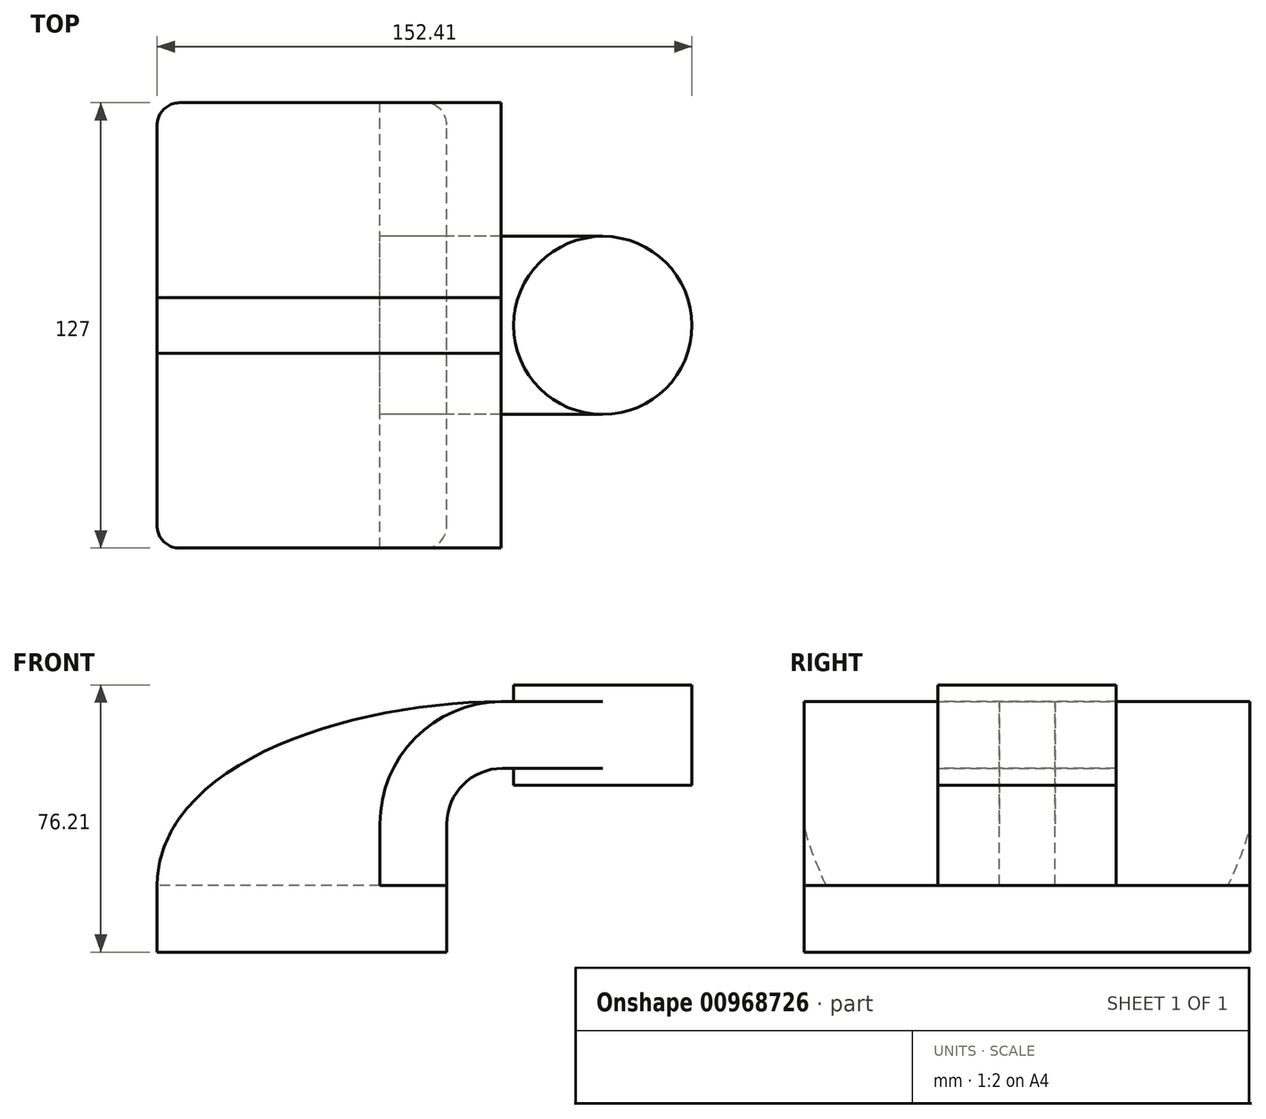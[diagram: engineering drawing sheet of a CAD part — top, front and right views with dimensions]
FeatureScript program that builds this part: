
annotation { "Feature Type Name" : "Feature", "Feature Type Description" : "" }
export const myFeature = defineFeature(function(context is Context, id is Id, definition is map)
    precondition{}
    {
        {
            var Q0;
            Q0=qCreatedBy(makeId("Front.planeOp"),FACE);
            var sketch = newSketch(context, id + "F0", { "sketchPlane" : qUnion([Q0])});
            skLineSegment(sketch, "E0.bottom", {"start": v(41.28, -9.52) * mm, "end": v(-41.28, -9.53) * mm});
            skLineSegment(sketch, "E0.top", {"start": v(41.28, 9.53) * mm, "end": v(-41.28, 9.53) * mm});
            skLineSegment(sketch, "E0.left", {"start": v(41.28, -9.52) * mm, "end": v(41.28, 9.53) * mm});
            skLineSegment(sketch, "E0.right", {"start": v(-41.28, -9.53) * mm, "end": v(-41.28, 9.53) * mm});
            skPoint(sketch, "E0.middle", {"position": v(0, 0) * mm});
            skLineSegment(sketch, "E1.bottom", {"start": v(111.12, 38.1) * mm, "end": v(60.33, 38.1) * mm});
            skLineSegment(sketch, "E1.top", {"start": v(111.12, 66.68) * mm, "end": v(60.33, 66.68) * mm});
            skLineSegment(sketch, "E1.left", {"start": v(111.12, 38.1) * mm, "end": v(111.12, 66.68) * mm});
            skLineSegment(sketch, "E1.right", {"start": v(60.33, 38.1) * mm, "end": v(60.33, 66.68) * mm});
            skPoint(sketch, "E1.middle", {"position": v(85.72, 52.39) * mm});
            skLineSegment(sketch, "E2", {"start": v(41.28, 9.53) * mm, "end": v(41.28, 27) * mm});
            skArc(sketch, "E3", {"start": v(41.27, 27) * mm, "mid": v(45.92, 38.23) * mm, "end": v(57.15, 42.88) * mm});
            skLineSegment(sketch, "E4", {"start": v(57.15, 42.88) * mm, "end": v(85.72, 42.88) * mm});
            skPoint(sketch, "E4.endSnap0", {"position": v(85.72, 38.1) * mm});
            skLineSegment(sketch, "E5.0", {"start": v(57.15, 61.93) * mm, "end": v(85.72, 61.93) * mm});
            skArc(sketch, "E5.1", {"start": v(22.23, 27) * mm, "mid": v(32.45, 51.7) * mm, "end": v(57.15, 61.93) * mm});
            skLineSegment(sketch, "E5.2", {"start": v(22.22, 9.53) * mm, "end": v(22.22, 27) * mm});
            skFitSpline(sketch, "E6", {"points": [v(-41.28, 9.53) * mm, v(57.15, 61.93) * mm], "startDerivative": vector(1.19, 104.94) * mm, "endDerivative": vector(132.12, 0.71) * mm});
            skLineSegment(sketch, "E7", {"start": v(85.72, 66.68) * mm, "end": v(85.72, 38.1) * mm});
            skSolve(sketch);
        }
        {
            var Q0;
            {var subQ0=sQuery(id+"F0.wireOp",EDGE,"E6");var subQ1=sQuery(id+"F0.wireOp",EDGE,"E5.1");var subQ3=makeQuery(id+"F0.imprint","INTERSECT",VERTEX,{"derivedFrom":[subQ1,subQ0]});Q0=makeQuery(id+"F0.imprint","IMPRINT",FACE,{"disambiguationData":[TD([[makeQuery(id+"F0.imprint","IMPRINT",EDGE,{"disambiguationData":[TD([[subQ3,-1.0]])],"derivedFrom":subQ1}),-1.0]])]});}
            var Q1;
            Q1=makeQuery(id+"F0.imprint","IMPRINT",FACE,{"disambiguationData":[TD([[makeQuery(id+"F0.imprint","IMPRINT",EDGE,{"derivedFrom":sQuery(id+"F0.wireOp",EDGE,"E0.bottom")}),-1.0]])]});
            extrude(context, id + "F1", {"entities" : qUnion([Q0, Q1]), "endBound" : BoundingType.SYMMETRIC, "depth" : 127 * mm, "offsetDistance" : 25.4 * mm});
        }
        {
            var Q0;
            {var subQ1=sQuery(id+"F0.wireOp",EDGE,"E2");Q0=makeQuery(id+"F0.imprint","IMPRINT",FACE,{"disambiguationData":[TD([[makeQuery(id+"F0.imprint","IMPRINT",EDGE,{"derivedFrom":subQ1}),1.0]])]});}
            var Q1;
            {var subQ0=sQuery(id+"F0.wireOp",EDGE,"E4");var subQ1=sQuery(id+"F0.wireOp",EDGE,"E1.right");var subQ2=makeQuery(id+"F0.imprint","INTERSECT",VERTEX,{"derivedFrom":[subQ1,subQ0]});Q1=makeQuery(id+"F0.imprint","IMPRINT",FACE,{"disambiguationData":[TD([[makeQuery(id+"F0.imprint","IMPRINT",EDGE,{"disambiguationData":[TD([[subQ2,-1.0]])],"derivedFrom":subQ1}),-1.0]])]});}
            extrude(context, id + "F2", {"entities" : qUnion([Q0, Q1]), "endBound" : BoundingType.SYMMETRIC, "depth" : 50.8 * mm, "offsetDistance" : 25.4 * mm});
        }
        {
            var Q0;
            {var subQ3=sQuery(id+"F0.wireOp",EDGE,"E5.2");Q0=makeQuery(id+"F0.imprint","IMPRINT",FACE,{"disambiguationData":[TD([[makeQuery(id+"F0.imprint","IMPRINT",EDGE,{"derivedFrom":subQ3}),1.0]])]});}
            extrude(context, id + "F3", {"entities" : qUnion([Q0]), "endBound" : BoundingType.SYMMETRIC, "depth" : 15.88 * mm, "offsetDistance" : 25.4 * mm});
        }
        {
            var Q0;
            {var subQ4=sQuery(id+"F0.wireOp",EDGE,"E1.left");Q0=makeQuery(id+"F0.imprint","IMPRINT",FACE,{"disambiguationData":[TD([[makeQuery(id+"F0.imprint","IMPRINT",EDGE,{"derivedFrom":subQ4}),1.0]])]});}
            var Q1;
            Q1=sQuery(id+"F0.wireOp",EDGE,"E7");
            revolve(context, id + "F4", {"operationType" : NewBodyOperationType.ADD, "surfaceOperationType" : NewSurfaceOperationType.NEW, "entities" : qUnion([Q0]), "axis" : qUnion([Q1]), "revolveType" : RevolveType.FULL});
        }
        {
            var Q0;
            Q0=makeQuery(id+"F1.opExtrude","CAP_EDGE",EDGE,{"disambiguationData":[OSD([sQuery(id+"F0.wireOp",EDGE,"E0.left")])],"isStart":false});
            var Q1;
            Q1=makeQuery(id+"F1.opExtrude","CAP_EDGE",EDGE,{"disambiguationData":[OSD([sQuery(id+"F0.wireOp",EDGE,"E0.right")])],"isStart":false});
            var Q2;
            Q2=makeQuery(id+"F1.opExtrude","CAP_EDGE",EDGE,{"disambiguationData":[OSD([sQuery(id+"F0.wireOp",EDGE,"E0.left")])],"isStart":true});
            var Q3;
            Q3=makeQuery(id+"F1.opExtrude","CAP_EDGE",EDGE,{"disambiguationData":[OSD([sQuery(id+"F0.wireOp",EDGE,"E0.right")])],"isStart":true});
            fillet(context, id + "F5", {"entities" : qUnion([Q0, Q1, Q2, Q3]), "radius" : 6.35 * mm, "tangentPropagation" : true, "allowEdgeOverflow" : false});
        }
    });
